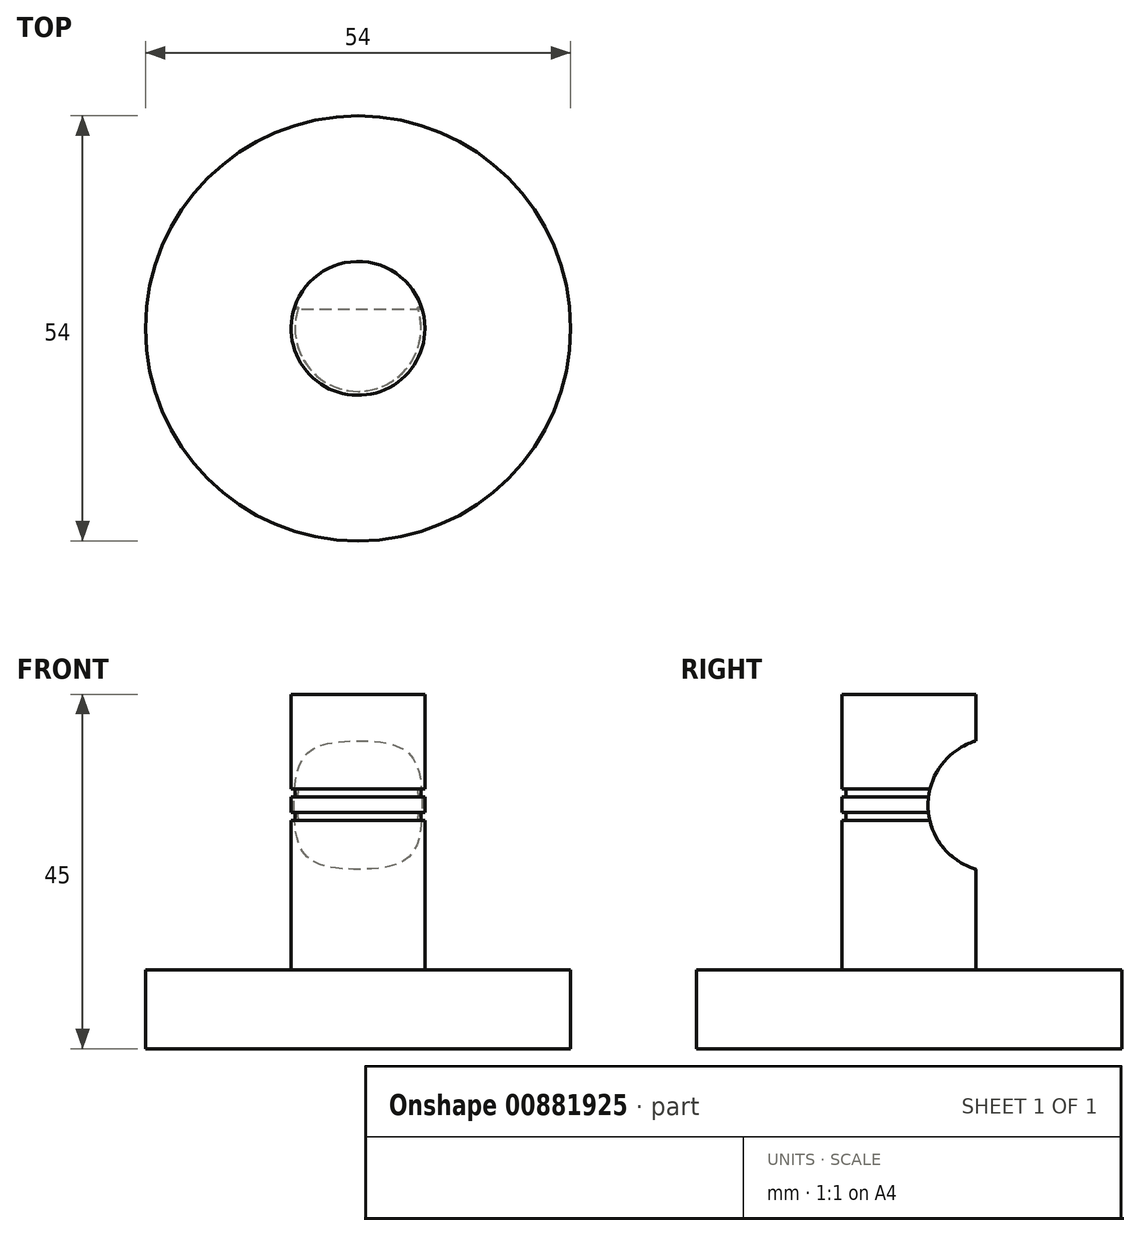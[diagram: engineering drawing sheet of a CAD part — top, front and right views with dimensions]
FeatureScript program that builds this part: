
annotation { "Feature Type Name" : "Feature", "Feature Type Description" : "" }
export const myFeature = defineFeature(function(context is Context, id is Id, definition is map)
    precondition{}
    {
        {
            var Q0;
            Q0=qCreatedBy(makeId("Top.planeOp"),FACE);
            var sketch = newSketch(context, id + "F0", { "sketchPlane" : qUnion([Q0])});
            skCircle(sketch, "E0", {"center": v(0, 0) * mm, "radius": 27 * mm});
            skSolve(sketch);
        }
        {
            var Q0;
            Q0=makeQuery(id+"F0.imprint","IMPRINT",FACE,{"disambiguationData":[TD([[makeQuery(id+"F0.imprint","IMPRINT",EDGE,{"derivedFrom":sQuery(id+"F0.wireOp",EDGE,"E0")}),1.0]])]});
            extrude(context, id + "F1", {"entities" : qUnion([Q0]), "depth" : 10 * mm, "offsetDistance" : 25 * mm});
        }
        {
            var Q0;
            Q0=makeQuery(id+"F1.opExtrude","CAP_FACE",FACE,{"disambiguationData":[OSD([sQuery(id+"F0.wireOp",EDGE,"E0")])],"isStart":false});
            var sketch = newSketch(context, id + "F2", { "sketchPlane" : qUnion([Q0])});
            skCircle(sketch, "E1", {"center": v(0, 0) * mm, "radius": 8.5 * mm});
            skSolve(sketch);
        }
        {
            var Q0;
            Q0=makeQuery(id+"F2.imprint","IMPRINT",FACE,{"disambiguationData":[TD([[makeQuery(id+"F2.imprint","IMPRINT",EDGE,{"derivedFrom":sQuery(id+"F2.wireOp",EDGE,"E1")}),1.0]])]});
            extrude(context, id + "F3", {"entities" : qUnion([Q0]), "depth" : 19 * mm, "offsetDistance" : 25 * mm});
        }
        {
            var Q0;
            Q0=makeQuery(id+"F3.opExtrude","CAP_FACE",FACE,{"disambiguationData":[OSD([sQuery(id+"F2.wireOp",EDGE,"E1")])],"isStart":false});
            var sketch = newSketch(context, id + "F4", { "sketchPlane" : qUnion([Q0])});
            skCircle(sketch, "E2", {"center": v(0, 0) * mm, "radius": 8 * mm});
            skSolve(sketch);
        }
        {
            var Q0;
            Q0 = qSketchRegion(id + "F4", true);
            extrude(context, id + "F5", {"entities" : qUnion([Q0]), "operationType" : NewBodyOperationType.ADD, "depth" : 1 * mm, "offsetDistance" : 25 * mm});
        }
        {
            var Q0;
            Q0=makeQuery(id+"F5.opExtrude","CAP_FACE",FACE,{"disambiguationData":[OSD([sQuery(id+"F4.wireOp",EDGE,"E2")])],"isStart":false});
            var sketch = newSketch(context, id + "F6", { "sketchPlane" : qUnion([Q0])});
            skCircle(sketch, "E3", {"center": v(0, 0) * mm, "radius": 8.5 * mm});
            skSolve(sketch);
        }
        {
            var Q0;
            Q0 = qSketchRegion(id + "F6", true);
            extrude(context, id + "F7", {"entities" : qUnion([Q0]), "operationType" : NewBodyOperationType.ADD, "depth" : 2 * mm, "offsetDistance" : 25 * mm});
        }
        {
            var Q0;
            Q0=makeQuery(id+"F7.opExtrude","CAP_FACE",FACE,{"disambiguationData":[OSD([sQuery(id+"F6.wireOp",EDGE,"E3")])],"isStart":false});
            var sketch = newSketch(context, id + "F8", { "sketchPlane" : qUnion([Q0])});
            skCircle(sketch, "E4", {"center": v(0, 0) * mm, "radius": 8 * mm});
            skSolve(sketch);
        }
        {
            var Q0;
            Q0 = qSketchRegion(id + "F8", true);
            extrude(context, id + "F9", {"entities" : qUnion([Q0]), "operationType" : NewBodyOperationType.ADD, "depth" : 1 * mm, "offsetDistance" : 25 * mm});
        }
        {
            var Q0;
            Q0=makeQuery(id+"F9.opExtrude","CAP_FACE",FACE,{"disambiguationData":[OSD([sQuery(id+"F8.wireOp",EDGE,"E4")])],"isStart":false});
            var sketch = newSketch(context, id + "F10", { "sketchPlane" : qUnion([Q0])});
            skCircle(sketch, "E5", {"center": v(0, 0) * mm, "radius": 8.5 * mm});
            skSolve(sketch);
        }
        {
            var Q0;
            Q0 = qSketchRegion(id + "F10", true);
            extrude(context, id + "F11", {"entities" : qUnion([Q0]), "operationType" : NewBodyOperationType.ADD, "depth" : 12 * mm, "offsetDistance" : 25 * mm});
        }
        {
            var Q0;
            Q0=qCreatedBy(makeId("Right.planeOp"),FACE);
            var sketch = newSketch(context, id + "F12", { "sketchPlane" : qUnion([Q0])});
            skCircle(sketch, "E6", {"center": v(10.9, 30.94) * mm, "radius": 8.5 * mm});
            skSolve(sketch);
        }
        {
            var Q0;
            Q0 = qSketchRegion(id + "F12", true);
            extrude(context, id + "F13", {"entities" : qUnion([Q0]), "operationType" : NewBodyOperationType.REMOVE, "endBound" : BoundingType.SYMMETRIC, "depth" : 25 * mm, "offsetDistance" : 25 * mm});
        }
    });
